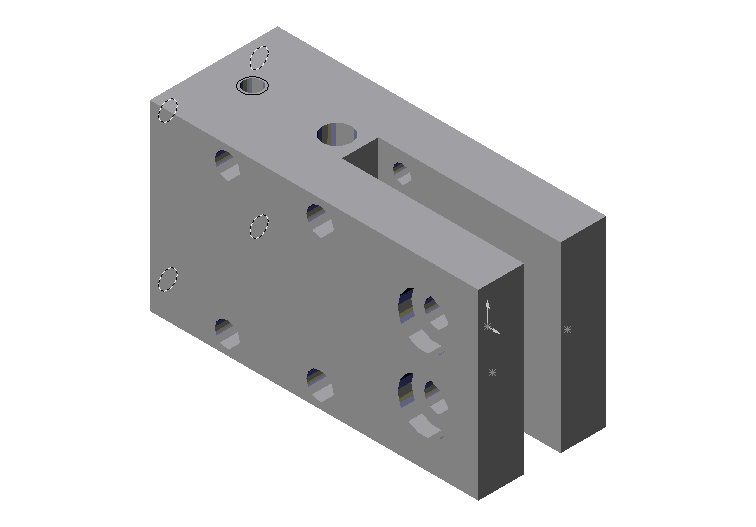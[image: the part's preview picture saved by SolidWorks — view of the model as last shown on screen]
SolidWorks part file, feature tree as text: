
SOLIDWORKS PART (.sldprt)
format: sldprt  version: not decoded by parser v0  size: 279,552 bytes
history: native  units: mm
features: sketch x16, cut_extrude x8, plane x6, mirror x4, hole x2, thread x2, material x1, extrude x1, cut_revolve x1 (+8 scaffold rows collapsed)
feature tree (49):
  scaffold x8  (default folders/planes/origin — collapsed)
  material  "Matériau <non spécifié>"
  plane  "Face"
  plane  "Dessus"
  plane  "Droite"
  sketch  "Esquisse1"  dims[c1.D3=4.0mm c1.D4=4.0mm c1.D5=4.0mm c1.D6=5.5mm c1.D7=4.0mm c1.D8=5.5mm c2.D5=5.5mm c2.D8=4.0mm c2.D10=4.0mm c2.D11=6.0mm c2.D7=4.0mm c3.D8=4.0mm c3.D10=4.0mm c4.D8=4.0mm c4.D1=40.0mm c4.D2=72.0mm c4.D3=16.0mm c4.D4=17.0mm c4.D5=4.5mm c4.D7=37.3mm c5.D8=32.0mm c5.D5=32.0mm c6.D8=31.2mm c6.D9=60.1mm c7.D8=37.3mm c7.D10=31.2mm c8.D8=22.8mm]
  extrude  "Base-Extrusion"  Depth=28mm
  sketch  "Esquisse2"  dims[c1.D1=~29.394704mm c1.D2=8.0mm c2.D1=28.0mm]
  cut_extrude  "Enlèv. mat.-Extru.1"  [1 undecoded]
  plane  "Plan1"  Offset=18.1mm
  sketch  "Esquisse16"  dims[D1=25.0mm]
  cut_extrude  "Enlèv. mat.-Extru.5"  [1 undecoded]
  plane  "Plan2"  Offset=58.6mm
  sketch  "Esquisse17"  dims[D1=27.0mm]
  cut_extrude  "Enlèv. mat.-Extru.6"  Depth=1.5mm
  sketch  "Esquisse18"  dims[D1=26.0mm]
  cut_extrude  "Enlèv. mat.-Extru.7"  Depth=5.4mm
  sketch  "Esquisse5"  dims[D1=6.0mm]
  cut_extrude  "Enlèv. mat.-Extru.2"  [1 undecoded]
  sketch  "Esquisse6"  dims[D1=11.6mm]
  cut_extrude  "Enlèv. mat.-Extru.3"  Depth=3mm
  mirror  "Symétrie1"
  sketch  "Esquisse7"  dims[D1=6.4mm D2=33.1mm]
  cut_extrude  "Enlèv. mat.-Extru.4"  [1 undecoded]
  hole  "Perçage1"  Diameter=2mm Depth=7.5mm
  sketch  "Esquisse10"  dims[D1=1.6mm]
  sketch  "Esquisse9"  dims[Diamètre=2.0mm Profondeur=7.5mm Diamètre contre-pointe=4.0mm Profondeur contre-pointe=6.0mm Angle=118.0deg Angle contre-pointe=118.0deg]
  thread  "Représentation de filetage1"  Diameter=4mm  [1 undecoded]
  sketch  "Esquisse13"  dims[c1.D1=8.25mm c1.D2=71.0mm c1.D3=3.4mm c1.D4=~3.587495mm c2.D4=60.0deg c2.D2=10.9mm]
  cut_revolve  "Enlèvement de matière-Révolution1"  Angle=360deg
  mirror  "Symétrie2"
  hole  "Perçage3"  Diameter=3.2mm Depth=10mm
  sketch  "Esquisse15"  dims[D1=16.0mm D2=10.0mm]
  sketch  "Esquisse14"  dims[c1.D1=~97.659253deg c1.D2=~82.982399deg c1.Diamètre=3.2mm c2.D2=100.0mm c2.D3=~82.982399deg c2.D4=90.0deg c3.D3=~97.716715deg c3.Profondeur=10.0mm c3.Angle=118.0deg]
  thread  "Représentation de filetage2"  Diameter=8mm  [1 undecoded]
  mirror  "Symétrie3"
  mirror  "Symétrie4"
  plane  "Plan3"  Offset=27.27mm
  sketch  "Point 1"
  sketch  "Point 2"
  sketch  "Esquisse19"  dims[D2=12.0mm D1=0.0mm]
  cut_extrude  "COUPE DU CORPS"  [1 undecoded]
decode coverage: 23 of 34 modeling features carry decoded parameters
note: ~ marks probable driven/reference dimensions
note: 7 parameter values undecoded
summary: no parameter record found for 5 features
note: suppression state not decoded; provenance and decode notes live in map.json
